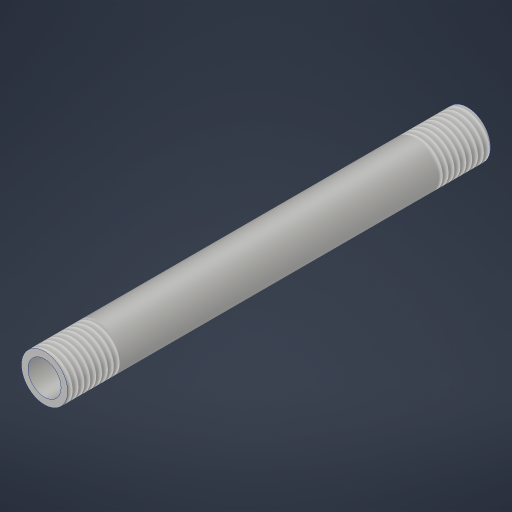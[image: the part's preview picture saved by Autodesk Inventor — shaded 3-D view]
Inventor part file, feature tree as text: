
AUTODESK INVENTOR PART (.ipt)
format: ipt  version: 2023.4 (Build 274418000, 418)  size: 200,192 bytes
history: native  units: in
note: dims shown in document units (in); Inventor stores cm internally (conversion verified against a paired STEP export)
features: thread x2, extrude x1, sketch x1
ambient origin geometry x8: Origin, YZ Plane, XZ Plane, XY Plane, X Axis, Y Axis, Z Axis, Center Point
bodies: Solid1 (feature_tree)
feature tree (4):
  extrude  "Extrusion1"  Depth=8.0in
  thread  "Thread1"  [1 undecoded]
  thread  "Thread2"  [1 undecoded]
  sketch  "Sketch1"  dims[d0=0.875in d1=0.125in d2=8.0in d3=0.0in d4=1.0in d5=0.0in d6=1.0in d7=0.0in]
note: 2 required parameter values undecoded (feature->parameter linkage not recoverable at this tier; creation-order binding heuristic only, values carry confidence <= 0.55)
